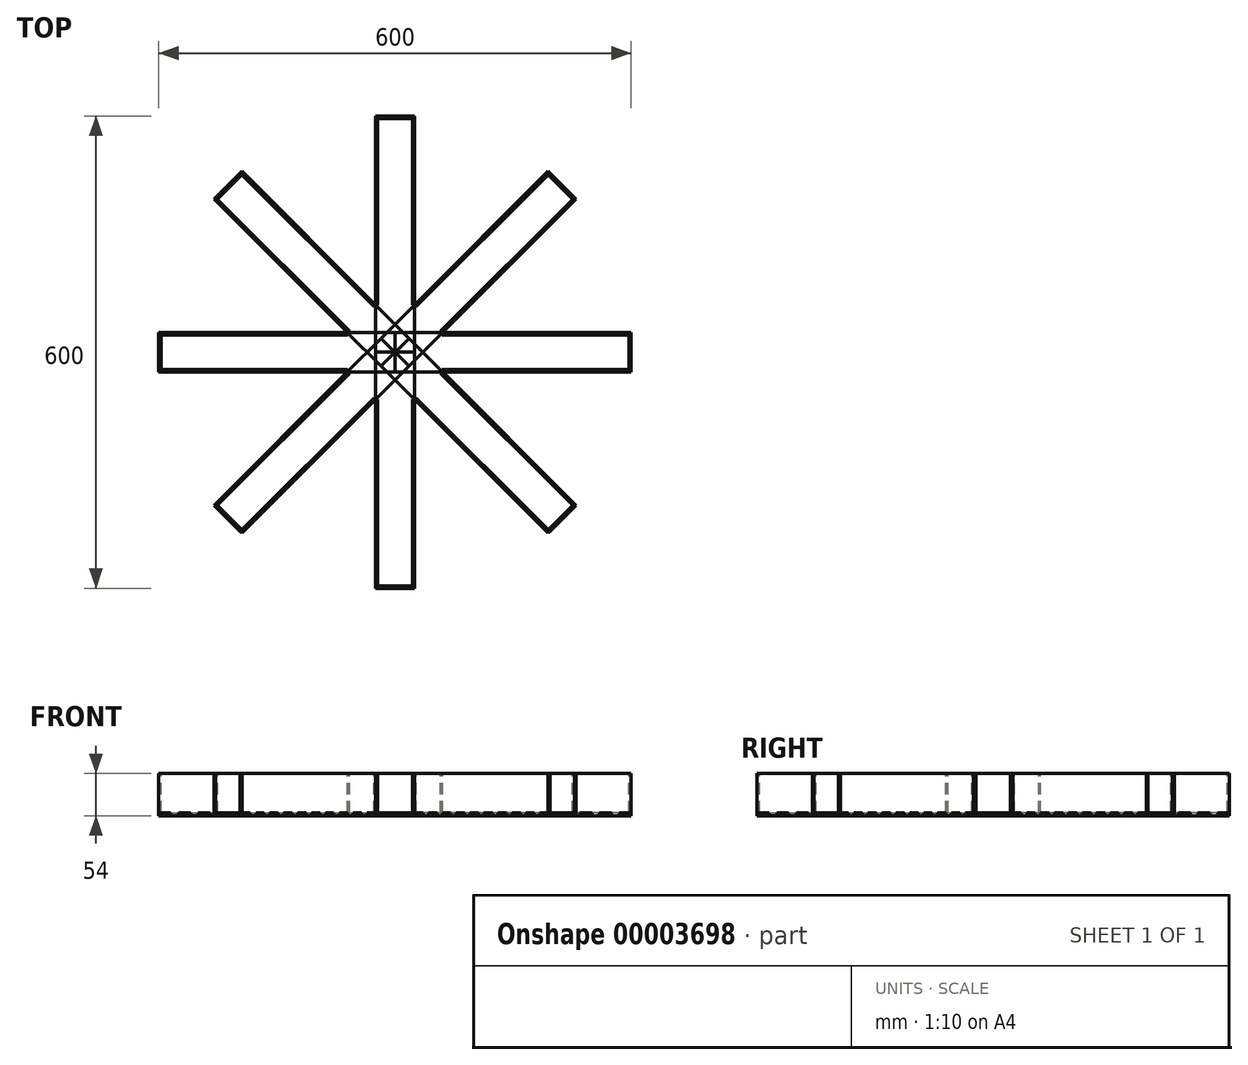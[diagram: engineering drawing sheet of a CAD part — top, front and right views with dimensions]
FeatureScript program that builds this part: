
annotation { "Feature Type Name" : "Feature", "Feature Type Description" : "" }
export const myFeature = defineFeature(function(context is Context, id is Id, definition is map)
    precondition{}
    {
        {
            var Q0;
            Q0=qCreatedBy(makeId("Top.planeOp"),FACE);
            var sketch = newSketch(context, id + "F0", { "sketchPlane" : qUnion([Q0])});
            skLineSegment(sketch, "E0.rect.bottom", {"start": v(-150, 25) * mm, "end": v(150, 25) * mm});
            skLineSegment(sketch, "E0.rect.top", {"start": v(-150, -25) * mm, "end": v(150, -25) * mm});
            skLineSegment(sketch, "E0.rect.left", {"start": v(-150, 25) * mm, "end": v(-150, -25) * mm});
            skLineSegment(sketch, "E0.rect.right", {"start": v(150, 25) * mm, "end": v(150, -25) * mm});
            skPoint(sketch, "E0.rect.middle", {"position": v(0, 0) * mm});
            skSolve(sketch);
        }
        {
            var Q0;
            Q0=makeQuery(id+"F0.imprint","IMPRINT",FACE,{"disambiguationData":[TD([[makeQuery(id+"F0.imprint","IMPRINT",EDGE,{"derivedFrom":sQuery(id+"F0.wireOp",EDGE,"E0.rect.bottom")}),-1.0]])]});
            extrude(context, id + "F1", {"entities" : qUnion([Q0]), "depth" : 4 * mm});
        }
        {
            var Q0;
            Q0=qCreatedBy(makeId("Front.planeOp"),FACE);
            var sketch = newSketch(context, id + "F2", { "sketchPlane" : qUnion([Q0])});
            skLineSegment(sketch, "E1", {"start": v(0, 0) * mm, "end": v(0, 104.2) * mm});
            skSolve(sketch);
        }
        {
            var Q0;
            Q0=makeQuery(id+"F1.opExtrude","SWEPT_FACE",FACE,{"disambiguationData":[OSD([sQuery(id+"F0.wireOp",EDGE,"E0.rect.top")])]});
            var sketch = newSketch(context, id + "F3", { "sketchPlane" : qUnion([Q0])});
            skLineSegment(sketch, "E2.bottom", {"start": v(-150, 4) * mm, "end": v(-135, 4) * mm});
            skLineSegment(sketch, "E2.top", {"start": v(-150, 54) * mm, "end": v(90, 54) * mm});
            skLineSegment(sketch, "E2.left", {"start": v(-150, 4) * mm, "end": v(-150, 54) * mm});
            skLineSegment(sketch, "E2.right", {"start": v(90, 4) * mm, "end": v(90, 54) * mm});
            skLineSegment(sketch, "E3.top", {"start": v(-135, 0) * mm, "end": v(-125, 0) * mm});
            skLineSegment(sketch, "E3.left", {"start": v(-135, 4) * mm, "end": v(-135, 0) * mm});
            skLineSegment(sketch, "E3.right", {"start": v(-125, 4) * mm, "end": v(-125, 0) * mm});
            skLineSegment(sketch, "E4.1.0.1", {"start": v(-110, 4) * mm, "end": v(-110, 0) * mm});
            skLineSegment(sketch, "E4.1.0.2", {"start": v(-100, 4) * mm, "end": v(-100, 0) * mm});
            skLineSegment(sketch, "E4.1.0.3", {"start": v(-110, 0) * mm, "end": v(-100, 0) * mm});
            skLineSegment(sketch, "E4.2.0.1", {"start": v(-85, 4) * mm, "end": v(-85, 0) * mm});
            skLineSegment(sketch, "E4.2.0.2", {"start": v(-75, 4) * mm, "end": v(-75, 0) * mm});
            skLineSegment(sketch, "E4.2.0.3", {"start": v(-85, 0) * mm, "end": v(-75, 0) * mm});
            skLineSegment(sketch, "E4.3.0.1", {"start": v(-60, 4) * mm, "end": v(-60, 0) * mm});
            skLineSegment(sketch, "E4.3.0.2", {"start": v(-50, 4) * mm, "end": v(-50, 0) * mm});
            skLineSegment(sketch, "E4.3.0.3", {"start": v(-60, 0) * mm, "end": v(-50, 0) * mm});
            skLineSegment(sketch, "E4.4.0.1", {"start": v(-35, 4) * mm, "end": v(-35, 0) * mm});
            skLineSegment(sketch, "E4.4.0.2", {"start": v(-25, 4) * mm, "end": v(-25, 0) * mm});
            skLineSegment(sketch, "E4.4.0.3", {"start": v(-35, 0) * mm, "end": v(-25, 0) * mm});
            skLineSegment(sketch, "E4.5.0.1", {"start": v(-10, 4) * mm, "end": v(-10, 0) * mm});
            skLineSegment(sketch, "E4.5.0.2", {"start": v(0, 4) * mm, "end": v(0, 0) * mm});
            skLineSegment(sketch, "E4.5.0.3", {"start": v(-10, 0) * mm, "end": v(0, 0) * mm});
            skLineSegment(sketch, "E4.6.0.1", {"start": v(15, 4) * mm, "end": v(15, 0) * mm});
            skLineSegment(sketch, "E4.6.0.2", {"start": v(25, 4) * mm, "end": v(25, 0) * mm});
            skLineSegment(sketch, "E4.6.0.3", {"start": v(15, 0) * mm, "end": v(25, 0) * mm});
            skLineSegment(sketch, "E4.7.0.1", {"start": v(40, 4) * mm, "end": v(40, 0) * mm});
            skLineSegment(sketch, "E4.7.0.2", {"start": v(50, 4) * mm, "end": v(50, 0) * mm});
            skLineSegment(sketch, "E4.7.0.3", {"start": v(40, 0) * mm, "end": v(50, 0) * mm});
            skLineSegment(sketch, "E4.8.0.1", {"start": v(65, 4) * mm, "end": v(65, 0) * mm});
            skLineSegment(sketch, "E4.8.0.2", {"start": v(75, 4) * mm, "end": v(75, 0) * mm});
            skLineSegment(sketch, "E4.8.0.3", {"start": v(65, 0) * mm, "end": v(75, 0) * mm});
            skLineSegment(sketch, "E4.direction1", {"start": v(-135, 4) * mm, "end": v(-110, 4) * mm, "construction": true});
            skLineSegment(sketch, "E5.trimOffspring", {"start": v(-125, 4) * mm, "end": v(-110, 4) * mm});
            skLineSegment(sketch, "E6.trimOffspring", {"start": v(-100, 4) * mm, "end": v(-85, 4) * mm});
            skLineSegment(sketch, "E7.trimOffspring", {"start": v(-75, 4) * mm, "end": v(-60, 4) * mm});
            skLineSegment(sketch, "E8.trimOffspring", {"start": v(-50, 4) * mm, "end": v(-35, 4) * mm});
            skLineSegment(sketch, "E9.trimOffspring", {"start": v(-25, 4) * mm, "end": v(-10, 4) * mm});
            skLineSegment(sketch, "E10.trimOffspring", {"start": v(0, 4) * mm, "end": v(15, 4) * mm});
            skLineSegment(sketch, "E11.trimOffspring", {"start": v(25, 4) * mm, "end": v(40, 4) * mm});
            skLineSegment(sketch, "E12.trimOffspring", {"start": v(50, 4) * mm, "end": v(65, 4) * mm});
            skLineSegment(sketch, "E13.trimOffspring", {"start": v(75, 4) * mm, "end": v(90, 4) * mm});
            skSolve(sketch);
        }
        {
            var Q0;
            {var subQ3=sQuery(id+"F3.wireOp",EDGE,"E2.bottom");var subQ8=sQuery(id+"F3.wireOp",EDGE,"E4.1.0.1");var subQ12=sQuery(id+"F3.wireOp",EDGE,"E4.2.0.1");var subQ16=sQuery(id+"F3.wireOp",EDGE,"E4.3.0.1");var subQ20=sQuery(id+"F3.wireOp",EDGE,"E4.4.0.1");var subQ24=sQuery(id+"F3.wireOp",EDGE,"E4.5.0.1");var subQ28=sQuery(id+"F3.wireOp",EDGE,"E4.6.0.1");var subQ32=sQuery(id+"F3.wireOp",EDGE,"E4.7.0.1");var subQ36=sQuery(id+"F3.wireOp",EDGE,"E4.8.0.1");Q0=qUnion([makeQuery(id+"F3.imprint","IMPRINT",FACE,{"disambiguationData":[TD([[makeQuery(id+"F3.imprint","IMPRINT",EDGE,{"derivedFrom":sQuery(id+"F3.wireOp",EDGE,"E3.top")}),1.0]])]}),makeQuery(id+"F3.imprint","IMPRINT",FACE,{"disambiguationData":[TD([[makeQuery(id+"F3.imprint","IMPRINT",EDGE,{"derivedFrom":subQ8}),1.0]])]}),makeQuery(id+"F3.imprint","IMPRINT",FACE,{"disambiguationData":[TD([[makeQuery(id+"F3.imprint","IMPRINT",EDGE,{"derivedFrom":subQ12}),1.0]])]}),makeQuery(id+"F3.imprint","IMPRINT",FACE,{"disambiguationData":[TD([[makeQuery(id+"F3.imprint","IMPRINT",EDGE,{"derivedFrom":subQ16}),1.0]])]}),makeQuery(id+"F3.imprint","IMPRINT",FACE,{"disambiguationData":[TD([[makeQuery(id+"F3.imprint","IMPRINT",EDGE,{"derivedFrom":subQ20}),1.0]])]}),makeQuery(id+"F3.imprint","IMPRINT",FACE,{"disambiguationData":[TD([[makeQuery(id+"F3.imprint","IMPRINT",EDGE,{"derivedFrom":subQ24}),1.0]])]}),makeQuery(id+"F3.imprint","IMPRINT",FACE,{"disambiguationData":[TD([[makeQuery(id+"F3.imprint","IMPRINT",EDGE,{"derivedFrom":subQ28}),1.0]])]}),makeQuery(id+"F3.imprint","IMPRINT",FACE,{"disambiguationData":[TD([[makeQuery(id+"F3.imprint","IMPRINT",EDGE,{"derivedFrom":subQ32}),1.0]])]}),makeQuery(id+"F3.imprint","IMPRINT",FACE,{"disambiguationData":[TD([[makeQuery(id+"F3.imprint","IMPRINT",EDGE,{"derivedFrom":subQ36}),1.0]])]}),makeQuery(id+"F3.imprint","IMPRINT",FACE,{"disambiguationData":[TD([[makeQuery(id+"F3.imprint","IMPRINT",EDGE,{"derivedFrom":subQ3}),1.0]])]})]);}
            extrude(context, id + "F4", {"entities" : qUnion([Q0]), "oppositeDirection" : true, "depth" : 3 * mm});
        }
        {
            var Q0;
            Q0=makeQuery(id+"F4.opExtrude","SWEPT_BODY",BODY,{"disambiguationData":[OSD([sQuery(id+"F3.wireOp",EDGE,"E2.bottom"),sQuery(id+"F3.wireOp",EDGE,"E2.top"),sQuery(id+"F3.wireOp",EDGE,"E2.left"),sQuery(id+"F3.wireOp",EDGE,"E2.right"),sQuery(id+"F3.wireOp",EDGE,"E3.top"),sQuery(id+"F3.wireOp",EDGE,"E3.left"),sQuery(id+"F3.wireOp",EDGE,"E3.right"),sQuery(id+"F3.wireOp",EDGE,"E4.1.0.1"),sQuery(id+"F3.wireOp",EDGE,"E4.1.0.2"),sQuery(id+"F3.wireOp",EDGE,"E4.1.0.3"),sQuery(id+"F3.wireOp",EDGE,"E4.2.0.1"),sQuery(id+"F3.wireOp",EDGE,"E4.2.0.2"),sQuery(id+"F3.wireOp",EDGE,"E4.2.0.3"),sQuery(id+"F3.wireOp",EDGE,"E4.3.0.1"),sQuery(id+"F3.wireOp",EDGE,"E4.3.0.2"),sQuery(id+"F3.wireOp",EDGE,"E4.3.0.3"),sQuery(id+"F3.wireOp",EDGE,"E4.4.0.1"),sQuery(id+"F3.wireOp",EDGE,"E4.4.0.2"),sQuery(id+"F3.wireOp",EDGE,"E4.4.0.3"),sQuery(id+"F3.wireOp",EDGE,"E4.5.0.1"),sQuery(id+"F3.wireOp",EDGE,"E4.5.0.2"),sQuery(id+"F3.wireOp",EDGE,"E4.5.0.3"),sQuery(id+"F3.wireOp",EDGE,"E4.6.0.1"),sQuery(id+"F3.wireOp",EDGE,"E4.6.0.2"),sQuery(id+"F3.wireOp",EDGE,"E4.6.0.3"),sQuery(id+"F3.wireOp",EDGE,"E4.7.0.1"),sQuery(id+"F3.wireOp",EDGE,"E4.7.0.2"),sQuery(id+"F3.wireOp",EDGE,"E4.7.0.3"),sQuery(id+"F3.wireOp",EDGE,"E4.8.0.1"),sQuery(id+"F3.wireOp",EDGE,"E4.8.0.2"),sQuery(id+"F3.wireOp",EDGE,"E4.8.0.3"),sQuery(id+"F3.wireOp",EDGE,"E5.trimOffspring"),sQuery(id+"F3.wireOp",EDGE,"E6.trimOffspring"),sQuery(id+"F3.wireOp",EDGE,"E7.trimOffspring"),sQuery(id+"F3.wireOp",EDGE,"E8.trimOffspring"),sQuery(id+"F3.wireOp",EDGE,"E9.trimOffspring"),sQuery(id+"F3.wireOp",EDGE,"E10.trimOffspring"),sQuery(id+"F3.wireOp",EDGE,"E11.trimOffspring"),sQuery(id+"F3.wireOp",EDGE,"E12.trimOffspring"),sQuery(id+"F3.wireOp",EDGE,"E13.trimOffspring")])]});
            var Q1;
            Q1=makeQuery(id+"F1.opExtrude","SWEPT_BODY",BODY,{"disambiguationData":[OSD([sQuery(id+"F0.wireOp",EDGE,"E0.rect.bottom"),sQuery(id+"F0.wireOp",EDGE,"E0.rect.top"),sQuery(id+"F0.wireOp",EDGE,"E0.rect.left"),sQuery(id+"F0.wireOp",EDGE,"E0.rect.right")])]});
            booleanBodies(context, id + "F5", {"operationType" : BooleanOperationType.SUBTRACTION, "tools" : qUnion([Q0]), "targets" : qUnion([Q1]), "keepTools" : true});
        }
        {
            var Q0;
            Q0=makeQuery(id+"F4.opExtrude","SWEPT_BODY",BODY,{"disambiguationData":[OSD([sQuery(id+"F3.wireOp",EDGE,"E2.bottom"),sQuery(id+"F3.wireOp",EDGE,"E2.top"),sQuery(id+"F3.wireOp",EDGE,"E2.left"),sQuery(id+"F3.wireOp",EDGE,"E2.right"),sQuery(id+"F3.wireOp",EDGE,"E3.top"),sQuery(id+"F3.wireOp",EDGE,"E3.left"),sQuery(id+"F3.wireOp",EDGE,"E3.right"),sQuery(id+"F3.wireOp",EDGE,"E4.1.0.1"),sQuery(id+"F3.wireOp",EDGE,"E4.1.0.2"),sQuery(id+"F3.wireOp",EDGE,"E4.1.0.3"),sQuery(id+"F3.wireOp",EDGE,"E4.2.0.1"),sQuery(id+"F3.wireOp",EDGE,"E4.2.0.2"),sQuery(id+"F3.wireOp",EDGE,"E4.2.0.3"),sQuery(id+"F3.wireOp",EDGE,"E4.3.0.1"),sQuery(id+"F3.wireOp",EDGE,"E4.3.0.2"),sQuery(id+"F3.wireOp",EDGE,"E4.3.0.3"),sQuery(id+"F3.wireOp",EDGE,"E4.4.0.1"),sQuery(id+"F3.wireOp",EDGE,"E4.4.0.2"),sQuery(id+"F3.wireOp",EDGE,"E4.4.0.3"),sQuery(id+"F3.wireOp",EDGE,"E4.5.0.1"),sQuery(id+"F3.wireOp",EDGE,"E4.5.0.2"),sQuery(id+"F3.wireOp",EDGE,"E4.5.0.3"),sQuery(id+"F3.wireOp",EDGE,"E4.6.0.1"),sQuery(id+"F3.wireOp",EDGE,"E4.6.0.2"),sQuery(id+"F3.wireOp",EDGE,"E4.6.0.3"),sQuery(id+"F3.wireOp",EDGE,"E4.7.0.1"),sQuery(id+"F3.wireOp",EDGE,"E4.7.0.2"),sQuery(id+"F3.wireOp",EDGE,"E4.7.0.3"),sQuery(id+"F3.wireOp",EDGE,"E4.8.0.1"),sQuery(id+"F3.wireOp",EDGE,"E4.8.0.2"),sQuery(id+"F3.wireOp",EDGE,"E4.8.0.3"),sQuery(id+"F3.wireOp",EDGE,"E5.trimOffspring"),sQuery(id+"F3.wireOp",EDGE,"E6.trimOffspring"),sQuery(id+"F3.wireOp",EDGE,"E7.trimOffspring"),sQuery(id+"F3.wireOp",EDGE,"E8.trimOffspring"),sQuery(id+"F3.wireOp",EDGE,"E9.trimOffspring"),sQuery(id+"F3.wireOp",EDGE,"E10.trimOffspring"),sQuery(id+"F3.wireOp",EDGE,"E11.trimOffspring"),sQuery(id+"F3.wireOp",EDGE,"E12.trimOffspring"),sQuery(id+"F3.wireOp",EDGE,"E13.trimOffspring")])]});
            var Q1;
            Q1=makeQuery(id+"F4.opExtrude","CAP_VERTEX",VERTEX,{"disambiguationData":[OSD([sQuery(id+"F0.wireOp",EDGE,"E0.rect.top"),sQuery(id+"F0.wireOp",EDGE,"E0.rect.left"),sQuery(id+"F3.wireOp",EDGE,"E2.bottom"),sQuery(id+"F3.wireOp",EDGE,"E2.left")])],"isStart":false});
            var Q2;
            Q2=makeQuery(id+"F1.opExtrude","CAP_VERTEX",VERTEX,{"disambiguationData":[OSD([sQuery(id+"F0.wireOp",EDGE,"E0.rect.bottom"),sQuery(id+"F0.wireOp",EDGE,"E0.rect.left")])],"isStart":false});
            transform(context, id + "F6", {"entities" : qUnion([Q0]), "transformType" : TransformType.TRANSLATION_ENTITY, "oppositeDirectionEntity" : false, "transformLine" : qUnion([Q1, Q2]), "makeCopy" : true});
        }
        {
            var Q0;
            Q0=makeQuery(id+"F6.opPattern","COPY",BODY,{"derivedFrom":makeQuery(id+"F4.opExtrude","SWEPT_BODY",BODY,{"disambiguationData":[OSD([sQuery(id+"F3.wireOp",EDGE,"E2.bottom"),sQuery(id+"F3.wireOp",EDGE,"E2.top"),sQuery(id+"F3.wireOp",EDGE,"E2.left"),sQuery(id+"F3.wireOp",EDGE,"E2.right"),sQuery(id+"F3.wireOp",EDGE,"E3.top"),sQuery(id+"F3.wireOp",EDGE,"E3.left"),sQuery(id+"F3.wireOp",EDGE,"E3.right"),sQuery(id+"F3.wireOp",EDGE,"E4.1.0.1"),sQuery(id+"F3.wireOp",EDGE,"E4.1.0.2"),sQuery(id+"F3.wireOp",EDGE,"E4.1.0.3"),sQuery(id+"F3.wireOp",EDGE,"E4.2.0.1"),sQuery(id+"F3.wireOp",EDGE,"E4.2.0.2"),sQuery(id+"F3.wireOp",EDGE,"E4.2.0.3"),sQuery(id+"F3.wireOp",EDGE,"E4.3.0.1"),sQuery(id+"F3.wireOp",EDGE,"E4.3.0.2"),sQuery(id+"F3.wireOp",EDGE,"E4.3.0.3"),sQuery(id+"F3.wireOp",EDGE,"E4.4.0.1"),sQuery(id+"F3.wireOp",EDGE,"E4.4.0.2"),sQuery(id+"F3.wireOp",EDGE,"E4.4.0.3"),sQuery(id+"F3.wireOp",EDGE,"E4.5.0.1"),sQuery(id+"F3.wireOp",EDGE,"E4.5.0.2"),sQuery(id+"F3.wireOp",EDGE,"E4.5.0.3"),sQuery(id+"F3.wireOp",EDGE,"E4.6.0.1"),sQuery(id+"F3.wireOp",EDGE,"E4.6.0.2"),sQuery(id+"F3.wireOp",EDGE,"E4.6.0.3"),sQuery(id+"F3.wireOp",EDGE,"E4.7.0.1"),sQuery(id+"F3.wireOp",EDGE,"E4.7.0.2"),sQuery(id+"F3.wireOp",EDGE,"E4.7.0.3"),sQuery(id+"F3.wireOp",EDGE,"E4.8.0.1"),sQuery(id+"F3.wireOp",EDGE,"E4.8.0.2"),sQuery(id+"F3.wireOp",EDGE,"E4.8.0.3"),sQuery(id+"F3.wireOp",EDGE,"E5.trimOffspring"),sQuery(id+"F3.wireOp",EDGE,"E6.trimOffspring"),sQuery(id+"F3.wireOp",EDGE,"E7.trimOffspring"),sQuery(id+"F3.wireOp",EDGE,"E8.trimOffspring"),sQuery(id+"F3.wireOp",EDGE,"E9.trimOffspring"),sQuery(id+"F3.wireOp",EDGE,"E10.trimOffspring"),sQuery(id+"F3.wireOp",EDGE,"E11.trimOffspring"),sQuery(id+"F3.wireOp",EDGE,"E12.trimOffspring"),sQuery(id+"F3.wireOp",EDGE,"E13.trimOffspring")])]}),"instanceName":"1"});
            var Q1;
            Q1=makeQuery(id+"F1.opExtrude","SWEPT_BODY",BODY,{"disambiguationData":[OSD([sQuery(id+"F0.wireOp",EDGE,"E0.rect.bottom"),sQuery(id+"F0.wireOp",EDGE,"E0.rect.top"),sQuery(id+"F0.wireOp",EDGE,"E0.rect.left"),sQuery(id+"F0.wireOp",EDGE,"E0.rect.right")])]});
            booleanBodies(context, id + "F7", {"operationType" : BooleanOperationType.SUBTRACTION, "tools" : qUnion([Q0]), "targets" : qUnion([Q1]), "keepTools" : true});
        }
        {
            var Q0;
            Q0=makeQuery(id+"F1.opExtrude","SWEPT_FACE",FACE,{"disambiguationData":[OSD([sQuery(id+"F0.wireOp",EDGE,"E0.rect.right")])]});
            var sketch = newSketch(context, id + "F8", { "sketchPlane" : qUnion([Q0])});
            skLineSegment(sketch, "E14", {"start": v(0, 4) * mm, "end": v(0, 32.45) * mm});
            skSolve(sketch);
        }
        {
            var Q0;
            Q0=makeQuery(id+"F1.opExtrude","SWEPT_FACE",FACE,{"disambiguationData":[OSD([sQuery(id+"F0.wireOp",EDGE,"E0.rect.left")])]});
            var sketch = newSketch(context, id + "F9", { "sketchPlane" : qUnion([Q0])});
            skLineSegment(sketch, "E15.0", {"start": v(-22, 4) * mm, "end": v(-22, 54) * mm});
            skLineSegment(sketch, "E16.0", {"start": v(22, 4) * mm, "end": v(22, 54) * mm});
            skLineSegment(sketch, "E17.bottom", {"start": v(-22, 54) * mm, "end": v(22, 54) * mm});
            skLineSegment(sketch, "E17.top", {"start": v(-22, 4) * mm, "end": v(22, 4) * mm});
            skLineSegment(sketch, "E17.left", {"start": v(-22, 54) * mm, "end": v(-22, 4) * mm});
            skLineSegment(sketch, "E17.right", {"start": v(22, 54) * mm, "end": v(22, 4) * mm});
            skSolve(sketch);
        }
        {
            var Q0;
            Q0=makeQuery(id+"F9.imprint","IMPRINT",FACE,{"disambiguationData":[TD([[makeQuery(id+"F9.imprint","IMPRINT",EDGE,{"derivedFrom":sQuery(id+"F9.wireOp",EDGE,"E17.bottom")}),-1.0]])]});
            extrude(context, id + "F10", {"entities" : qUnion([Q0]), "oppositeDirection" : true, "depth" : 3 * mm});
        }
        {
            var Q0;
            Q0=makeQuery(id+"F1.opExtrude","SWEPT_BODY",BODY,{"disambiguationData":[OSD([sQuery(id+"F0.wireOp",EDGE,"E0.rect.bottom"),sQuery(id+"F0.wireOp",EDGE,"E0.rect.top"),sQuery(id+"F0.wireOp",EDGE,"E0.rect.left"),sQuery(id+"F0.wireOp",EDGE,"E0.rect.right")])]});
            var Q1;
            Q1=makeQuery(id+"F6.opPattern","COPY",BODY,{"derivedFrom":makeQuery(id+"F4.opExtrude","SWEPT_BODY",BODY,{"disambiguationData":[OSD([sQuery(id+"F3.wireOp",EDGE,"E2.bottom"),sQuery(id+"F3.wireOp",EDGE,"E2.top"),sQuery(id+"F3.wireOp",EDGE,"E2.left"),sQuery(id+"F3.wireOp",EDGE,"E2.right"),sQuery(id+"F3.wireOp",EDGE,"E3.top"),sQuery(id+"F3.wireOp",EDGE,"E3.left"),sQuery(id+"F3.wireOp",EDGE,"E3.right"),sQuery(id+"F3.wireOp",EDGE,"E4.1.0.1"),sQuery(id+"F3.wireOp",EDGE,"E4.1.0.2"),sQuery(id+"F3.wireOp",EDGE,"E4.1.0.3"),sQuery(id+"F3.wireOp",EDGE,"E4.2.0.1"),sQuery(id+"F3.wireOp",EDGE,"E4.2.0.2"),sQuery(id+"F3.wireOp",EDGE,"E4.2.0.3"),sQuery(id+"F3.wireOp",EDGE,"E4.3.0.1"),sQuery(id+"F3.wireOp",EDGE,"E4.3.0.2"),sQuery(id+"F3.wireOp",EDGE,"E4.3.0.3"),sQuery(id+"F3.wireOp",EDGE,"E4.4.0.1"),sQuery(id+"F3.wireOp",EDGE,"E4.4.0.2"),sQuery(id+"F3.wireOp",EDGE,"E4.4.0.3"),sQuery(id+"F3.wireOp",EDGE,"E4.5.0.1"),sQuery(id+"F3.wireOp",EDGE,"E4.5.0.2"),sQuery(id+"F3.wireOp",EDGE,"E4.5.0.3"),sQuery(id+"F3.wireOp",EDGE,"E4.6.0.1"),sQuery(id+"F3.wireOp",EDGE,"E4.6.0.2"),sQuery(id+"F3.wireOp",EDGE,"E4.6.0.3"),sQuery(id+"F3.wireOp",EDGE,"E4.7.0.1"),sQuery(id+"F3.wireOp",EDGE,"E4.7.0.2"),sQuery(id+"F3.wireOp",EDGE,"E4.7.0.3"),sQuery(id+"F3.wireOp",EDGE,"E4.8.0.1"),sQuery(id+"F3.wireOp",EDGE,"E4.8.0.2"),sQuery(id+"F3.wireOp",EDGE,"E4.8.0.3"),sQuery(id+"F3.wireOp",EDGE,"E5.trimOffspring"),sQuery(id+"F3.wireOp",EDGE,"E6.trimOffspring"),sQuery(id+"F3.wireOp",EDGE,"E7.trimOffspring"),sQuery(id+"F3.wireOp",EDGE,"E8.trimOffspring"),sQuery(id+"F3.wireOp",EDGE,"E9.trimOffspring"),sQuery(id+"F3.wireOp",EDGE,"E10.trimOffspring"),sQuery(id+"F3.wireOp",EDGE,"E11.trimOffspring"),sQuery(id+"F3.wireOp",EDGE,"E12.trimOffspring"),sQuery(id+"F3.wireOp",EDGE,"E13.trimOffspring")])]}),"instanceName":"1"});
            var Q2;
            Q2=makeQuery(id+"F4.opExtrude","SWEPT_BODY",BODY,{"disambiguationData":[OSD([sQuery(id+"F3.wireOp",EDGE,"E2.bottom"),sQuery(id+"F3.wireOp",EDGE,"E2.top"),sQuery(id+"F3.wireOp",EDGE,"E2.left"),sQuery(id+"F3.wireOp",EDGE,"E2.right"),sQuery(id+"F3.wireOp",EDGE,"E3.top"),sQuery(id+"F3.wireOp",EDGE,"E3.left"),sQuery(id+"F3.wireOp",EDGE,"E3.right"),sQuery(id+"F3.wireOp",EDGE,"E4.1.0.1"),sQuery(id+"F3.wireOp",EDGE,"E4.1.0.2"),sQuery(id+"F3.wireOp",EDGE,"E4.1.0.3"),sQuery(id+"F3.wireOp",EDGE,"E4.2.0.1"),sQuery(id+"F3.wireOp",EDGE,"E4.2.0.2"),sQuery(id+"F3.wireOp",EDGE,"E4.2.0.3"),sQuery(id+"F3.wireOp",EDGE,"E4.3.0.1"),sQuery(id+"F3.wireOp",EDGE,"E4.3.0.2"),sQuery(id+"F3.wireOp",EDGE,"E4.3.0.3"),sQuery(id+"F3.wireOp",EDGE,"E4.4.0.1"),sQuery(id+"F3.wireOp",EDGE,"E4.4.0.2"),sQuery(id+"F3.wireOp",EDGE,"E4.4.0.3"),sQuery(id+"F3.wireOp",EDGE,"E4.5.0.1"),sQuery(id+"F3.wireOp",EDGE,"E4.5.0.2"),sQuery(id+"F3.wireOp",EDGE,"E4.5.0.3"),sQuery(id+"F3.wireOp",EDGE,"E4.6.0.1"),sQuery(id+"F3.wireOp",EDGE,"E4.6.0.2"),sQuery(id+"F3.wireOp",EDGE,"E4.6.0.3"),sQuery(id+"F3.wireOp",EDGE,"E4.7.0.1"),sQuery(id+"F3.wireOp",EDGE,"E4.7.0.2"),sQuery(id+"F3.wireOp",EDGE,"E4.7.0.3"),sQuery(id+"F3.wireOp",EDGE,"E4.8.0.1"),sQuery(id+"F3.wireOp",EDGE,"E4.8.0.2"),sQuery(id+"F3.wireOp",EDGE,"E4.8.0.3"),sQuery(id+"F3.wireOp",EDGE,"E5.trimOffspring"),sQuery(id+"F3.wireOp",EDGE,"E6.trimOffspring"),sQuery(id+"F3.wireOp",EDGE,"E7.trimOffspring"),sQuery(id+"F3.wireOp",EDGE,"E8.trimOffspring"),sQuery(id+"F3.wireOp",EDGE,"E9.trimOffspring"),sQuery(id+"F3.wireOp",EDGE,"E10.trimOffspring"),sQuery(id+"F3.wireOp",EDGE,"E11.trimOffspring"),sQuery(id+"F3.wireOp",EDGE,"E12.trimOffspring"),sQuery(id+"F3.wireOp",EDGE,"E13.trimOffspring")])]});
            var Q3;
            Q3=makeQuery(id+"F10.opExtrude","SWEPT_BODY",BODY,{"disambiguationData":[OSD([sQuery(id+"F9.wireOp",EDGE,"E17.bottom"),sQuery(id+"F9.wireOp",EDGE,"E17.top"),sQuery(id+"F9.wireOp",EDGE,"E17.left"),sQuery(id+"F9.wireOp",EDGE,"E17.right")])]});
            var Q4;
            Q4=sQuery(id+"F8.wireOp",EDGE,"E14");
            circularPattern(context, id + "F11", {"entities" : qUnion([Q0, Q1, Q2, Q3]), "axis" : qUnion([Q4]), "angle" : 45 * degree, "instanceCount" : 8});
        }
    });
